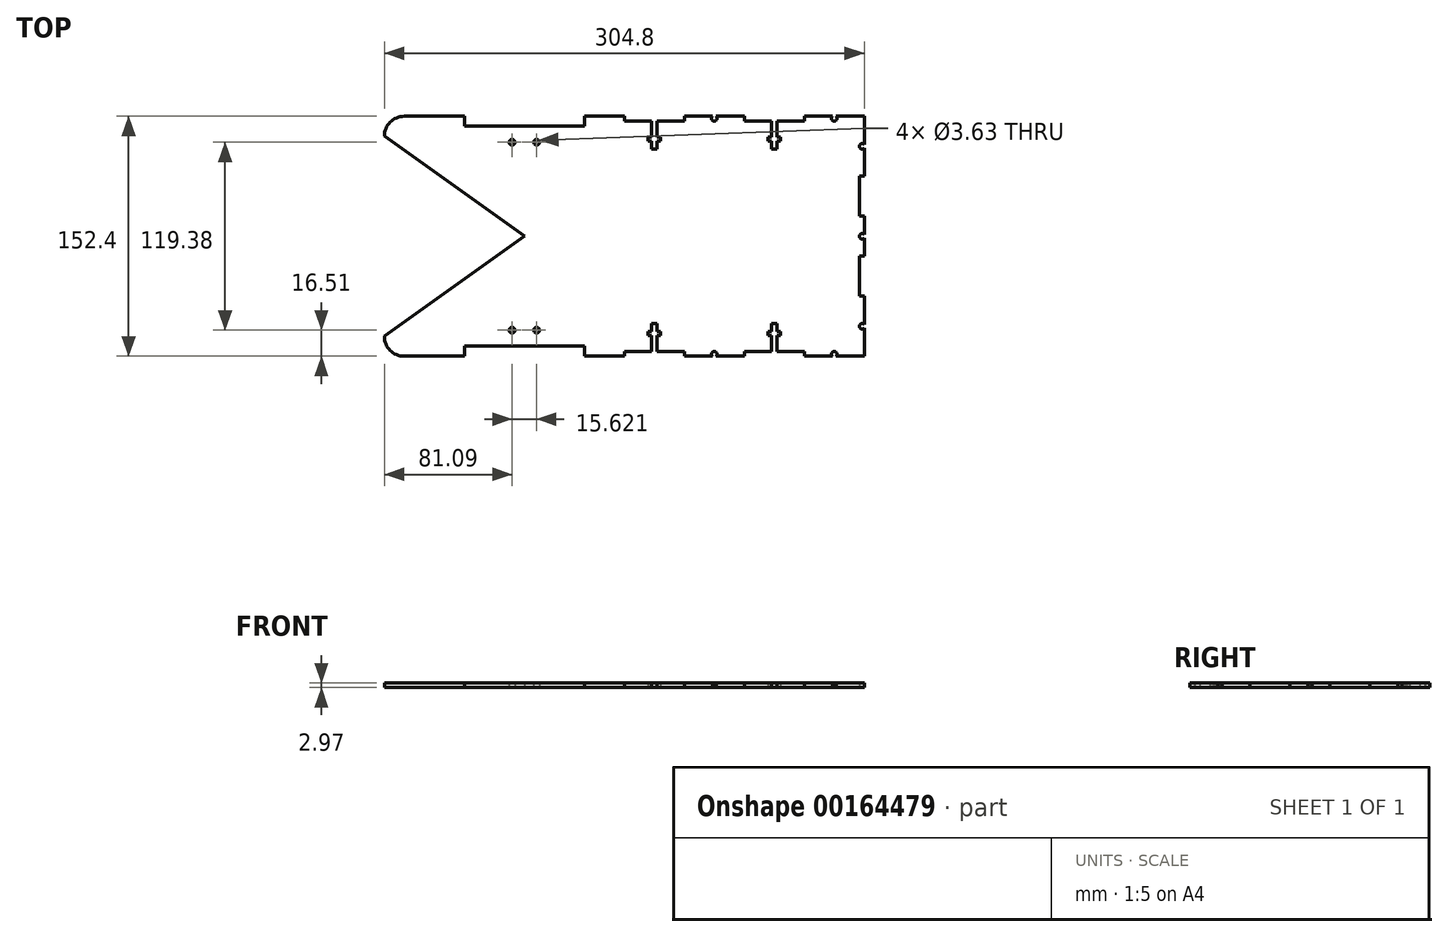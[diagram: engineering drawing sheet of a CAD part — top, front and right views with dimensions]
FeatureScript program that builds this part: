
annotation { "Feature Type Name" : "Feature", "Feature Type Description" : "" }
export const myFeature = defineFeature(function(context is Context, id is Id, definition is map)
    precondition{}
    {
        {
            var Q0;
            Q0=qCreatedBy(makeId("Top.planeOp"),FACE);
            var sketch = newSketch(context, id + "F0", { "sketchPlane" : qUnion([Q0])});
            skLineSegment(sketch, "E0.bottom", {"start": v(152.4, -76.2) * mm, "end": v(-139.7, -76.2) * mm});
            skLineSegment(sketch, "E0.top", {"start": v(152.4, 76.2) * mm, "end": v(-139.7, 76.2) * mm});
            skLineSegment(sketch, "E0.left", {"start": v(152.4, -76.2) * mm, "end": v(152.4, 76.2) * mm});
            skLineSegment(sketch, "E0.right", {"start": v(-152.4, -63.5) * mm, "end": v(-152.4, 63.5) * mm});
            skPoint(sketch, "E0.middle", {"position": v(0, 0) * mm});
            skLineSegment(sketch, "E1.bottom", {"start": v(-101.6, -76.2) * mm, "end": v(-25.4, -76.2) * mm});
            skLineSegment(sketch, "E1.top", {"start": v(-101.6, -69.85) * mm, "end": v(-25.4, -69.85) * mm});
            skLineSegment(sketch, "E1.left", {"start": v(-101.6, -76.2) * mm, "end": v(-101.6, -69.85) * mm});
            skLineSegment(sketch, "E1.right", {"start": v(-25.4, -76.2) * mm, "end": v(-25.4, -69.85) * mm});
            skLineSegment(sketch, "E2.bottom", {"start": v(0, -73.23) * mm, "end": v(17.28, -73.23) * mm});
            skLineSegment(sketch, "E2.top", {"start": v(0, -76.2) * mm, "end": v(38.1, -76.2) * mm});
            skLineSegment(sketch, "E2.left", {"start": v(0, -73.23) * mm, "end": v(0, -76.2) * mm});
            skLineSegment(sketch, "E2.right", {"start": v(38.1, -73.23) * mm, "end": v(38.1, -76.2) * mm});
            skLineSegment(sketch, "E3.bottom", {"start": v(17.28, -55.4) * mm, "end": v(20.82, -55.4) * mm});
            skLineSegment(sketch, "E3.top", {"start": v(17.28, -76.2) * mm, "end": v(20.82, -76.2) * mm});
            skLineSegment(sketch, "E3.left", {"start": v(17.28, -55.4) * mm, "end": v(17.28, -60.43) * mm});
            skLineSegment(sketch, "E3.right", {"start": v(20.82, -55.4) * mm, "end": v(20.82, -60.43) * mm});
            skPoint(sketch, "E4", {"position": v(19.05, -76.2) * mm});
            skLineSegment(sketch, "E5", {"start": v(19.05, -76.2) * mm, "end": v(19.05, -50.32) * mm, "construction": true});
            skLineSegment(sketch, "E6.bottom", {"start": v(22.94, -63.07) * mm, "end": v(20.82, -63.07) * mm});
            skLineSegment(sketch, "E6.top", {"start": v(22.94, -60.43) * mm, "end": v(20.82, -60.43) * mm});
            skLineSegment(sketch, "E6.left", {"start": v(22.94, -63.07) * mm, "end": v(22.94, -60.43) * mm});
            skLineSegment(sketch, "E6.right", {"start": v(15.16, -63.07) * mm, "end": v(15.16, -60.43) * mm});
            skPoint(sketch, "E6.middle", {"position": v(19.05, -61.75) * mm});
            skLineSegment(sketch, "E7.trimOffspring", {"start": v(20.82, -73.23) * mm, "end": v(38.1, -73.23) * mm});
            skLineSegment(sketch, "E8.trimOffspring", {"start": v(20.82, -63.07) * mm, "end": v(20.82, -73.23) * mm});
            skLineSegment(sketch, "E9.trimOffspring", {"start": v(17.28, -60.43) * mm, "end": v(15.16, -60.43) * mm});
            skLineSegment(sketch, "E10.trimOffspring", {"start": v(17.28, -63.07) * mm, "end": v(17.28, -73.23) * mm});
            skLineSegment(sketch, "E11.trimOffspring", {"start": v(17.28, -63.07) * mm, "end": v(15.16, -63.07) * mm});
            skArc(sketch, "E12", {"start": v(58.4, -76.2) * mm, "mid": v(57.15, -73.15) * mm, "end": v(55.9, -76.2) * mm});
            skLineSegment(sketch, "E13.1.0.0", {"start": v(93.48, -55.4) * mm, "end": v(93.48, -60.43) * mm});
            skPoint(sketch, "E13.1.0.1", {"position": v(95.25, -61.75) * mm});
            skLineSegment(sketch, "E13.1.0.2", {"start": v(97.02, -55.4) * mm, "end": v(97.02, -60.43) * mm});
            skArc(sketch, "E13.1.0.3", {"start": v(134.6, -76.2) * mm, "mid": v(133.35, -73.15) * mm, "end": v(132.1, -76.2) * mm});
            skLineSegment(sketch, "E13.1.0.4", {"start": v(93.48, -63.07) * mm, "end": v(93.48, -73.23) * mm});
            skLineSegment(sketch, "E13.1.0.5", {"start": v(97.02, -73.23) * mm, "end": v(114.3, -73.23) * mm});
            skLineSegment(sketch, "E13.1.0.6", {"start": v(76.2, -73.23) * mm, "end": v(93.48, -73.23) * mm});
            skLineSegment(sketch, "E13.1.0.7", {"start": v(76.2, -76.2) * mm, "end": v(114.3, -76.2) * mm});
            skLineSegment(sketch, "E13.1.0.8", {"start": v(97.02, -63.07) * mm, "end": v(97.02, -73.23) * mm});
            skLineSegment(sketch, "E13.1.0.9", {"start": v(95.25, -76.2) * mm, "end": v(95.25, -50.32) * mm, "construction": true});
            skPoint(sketch, "E13.1.0.10", {"position": v(95.25, -76.2) * mm});
            skLineSegment(sketch, "E13.1.0.11", {"start": v(93.48, -76.2) * mm, "end": v(97.02, -76.2) * mm});
            skLineSegment(sketch, "E13.1.0.12", {"start": v(99.14, -63.07) * mm, "end": v(97.02, -63.07) * mm});
            skLineSegment(sketch, "E13.1.0.13", {"start": v(99.14, -63.07) * mm, "end": v(99.14, -60.43) * mm});
            skLineSegment(sketch, "E13.1.0.14", {"start": v(91.36, -63.07) * mm, "end": v(91.36, -60.43) * mm});
            skLineSegment(sketch, "E13.1.0.15", {"start": v(93.48, -60.43) * mm, "end": v(91.36, -60.43) * mm});
            skLineSegment(sketch, "E13.1.0.16", {"start": v(99.14, -60.43) * mm, "end": v(97.02, -60.43) * mm});
            skLineSegment(sketch, "E13.1.0.17", {"start": v(76.2, -73.23) * mm, "end": v(76.2, -76.2) * mm});
            skLineSegment(sketch, "E13.1.0.18", {"start": v(114.3, -73.23) * mm, "end": v(114.3, -76.2) * mm});
            skLineSegment(sketch, "E13.1.0.19", {"start": v(93.48, -55.4) * mm, "end": v(97.02, -55.4) * mm});
            skLineSegment(sketch, "E13.1.0.20", {"start": v(93.48, -63.07) * mm, "end": v(91.36, -63.07) * mm});
            skLineSegment(sketch, "E13.direction1", {"start": v(0, -76.2) * mm, "end": v(76.2, -76.2) * mm, "construction": true});
            skLineSegment(sketch, "E14.MirrorCS", {"start": v(22.94, 63.07) * mm, "end": v(20.82, 63.07) * mm});
            skLineSegment(sketch, "E15.MirrorCS", {"start": v(22.94, 63.07) * mm, "end": v(22.94, 60.43) * mm});
            skLineSegment(sketch, "E16.MirrorCS", {"start": v(15.16, 63.07) * mm, "end": v(15.16, 60.43) * mm});
            skLineSegment(sketch, "E17.MirrorCS", {"start": v(17.28, 60.43) * mm, "end": v(15.16, 60.43) * mm});
            skLineSegment(sketch, "E18.MirrorCS", {"start": v(22.94, 60.43) * mm, "end": v(20.82, 60.43) * mm});
            skLineSegment(sketch, "E19.MirrorCS", {"start": v(99.14, 63.07) * mm, "end": v(99.14, 60.43) * mm});
            skLineSegment(sketch, "E20.MirrorCS", {"start": v(17.28, 63.07) * mm, "end": v(15.16, 63.07) * mm});
            skLineSegment(sketch, "E21.MirrorCS", {"start": v(99.14, 60.43) * mm, "end": v(97.02, 60.43) * mm});
            skLineSegment(sketch, "E22.MirrorCS", {"start": v(99.14, 63.07) * mm, "end": v(97.02, 63.07) * mm});
            skLineSegment(sketch, "E23.MirrorCS", {"start": v(93.48, 60.43) * mm, "end": v(91.36, 60.43) * mm});
            skLineSegment(sketch, "E24.MirrorCS", {"start": v(20.82, 55.4) * mm, "end": v(20.82, 60.43) * mm});
            skLineSegment(sketch, "E25.MirrorCS", {"start": v(76.2, 73.23) * mm, "end": v(76.2, 76.2) * mm});
            skLineSegment(sketch, "E26.MirrorCS", {"start": v(17.28, 55.4) * mm, "end": v(17.28, 60.43) * mm});
            skLineSegment(sketch, "E27.MirrorCS", {"start": v(0, 73.23) * mm, "end": v(0, 76.2) * mm});
            skLineSegment(sketch, "E28.MirrorCS", {"start": v(91.36, 63.07) * mm, "end": v(91.36, 60.43) * mm});
            skLineSegment(sketch, "E29.MirrorCS", {"start": v(93.48, 63.07) * mm, "end": v(91.36, 63.07) * mm});
            skLineSegment(sketch, "E30.MirrorCS", {"start": v(93.48, 55.4) * mm, "end": v(93.48, 60.43) * mm});
            skLineSegment(sketch, "E31.MirrorCS", {"start": v(97.02, 55.4) * mm, "end": v(97.02, 60.43) * mm});
            skLineSegment(sketch, "E32.MirrorCS", {"start": v(93.48, 55.4) * mm, "end": v(97.02, 55.4) * mm});
            skLineSegment(sketch, "E33.MirrorCS", {"start": v(-101.6, 76.2) * mm, "end": v(-101.6, 69.85) * mm});
            skLineSegment(sketch, "E34.MirrorCS", {"start": v(-25.4, 76.2) * mm, "end": v(-25.4, 69.85) * mm});
            skLineSegment(sketch, "E35.MirrorCS", {"start": v(38.1, 73.23) * mm, "end": v(38.1, 76.2) * mm});
            skLineSegment(sketch, "E36.MirrorCS", {"start": v(93.48, 76.2) * mm, "end": v(97.02, 76.2) * mm});
            skLineSegment(sketch, "E37.MirrorCS", {"start": v(114.3, 73.23) * mm, "end": v(114.3, 76.2) * mm});
            skLineSegment(sketch, "E38.MirrorCS", {"start": v(17.28, 55.4) * mm, "end": v(20.82, 55.4) * mm});
            skLineSegment(sketch, "E39.MirrorCS", {"start": v(17.28, 76.2) * mm, "end": v(20.82, 76.2) * mm});
            skLineSegment(sketch, "E40.MirrorCS", {"start": v(0, 76.2) * mm, "end": v(38.1, 76.2) * mm});
            skArc(sketch, "E41.MirrorCS", {"start": v(58.4, 76.2) * mm, "mid": v(57.15, 73.15) * mm, "end": v(55.9, 76.2) * mm});
            skArc(sketch, "E42.MirrorCS", {"start": v(134.6, 76.2) * mm, "mid": v(133.35, 73.15) * mm, "end": v(132.1, 76.2) * mm});
            skLineSegment(sketch, "E43.MirrorCS", {"start": v(97.02, 63.07) * mm, "end": v(97.02, 73.23) * mm});
            skLineSegment(sketch, "E44.MirrorCS", {"start": v(97.02, 73.23) * mm, "end": v(114.3, 73.23) * mm});
            skLineSegment(sketch, "E45.MirrorCS", {"start": v(20.82, 63.07) * mm, "end": v(20.82, 73.23) * mm});
            skPoint(sketch, "E46.MirrorP", {"position": v(95.25, 61.75) * mm});
            skPoint(sketch, "E47.MirrorP", {"position": v(19.05, 76.2) * mm});
            skLineSegment(sketch, "E48.MirrorCS", {"start": v(76.2, 76.2) * mm, "end": v(114.3, 76.2) * mm});
            skLineSegment(sketch, "E49.MirrorCS", {"start": v(93.48, 63.07) * mm, "end": v(93.48, 73.23) * mm});
            skLineSegment(sketch, "E50.MirrorCS", {"start": v(0, 76.2) * mm, "end": v(76.2, 76.2) * mm, "construction": true});
            skLineSegment(sketch, "E51.MirrorCS", {"start": v(20.82, 73.23) * mm, "end": v(38.1, 73.23) * mm});
            skLineSegment(sketch, "E52.MirrorCS", {"start": v(17.28, 63.07) * mm, "end": v(17.28, 73.23) * mm});
            skLineSegment(sketch, "E53.MirrorCS", {"start": v(76.2, 73.23) * mm, "end": v(93.48, 73.23) * mm});
            skPoint(sketch, "E54.MirrorP", {"position": v(95.25, 76.2) * mm});
            skLineSegment(sketch, "E55.MirrorCS", {"start": v(-101.6, 76.2) * mm, "end": v(-25.4, 76.2) * mm});
            skLineSegment(sketch, "E56.MirrorCS", {"start": v(-101.6, 69.85) * mm, "end": v(-25.4, 69.85) * mm});
            skLineSegment(sketch, "E57.MirrorCS", {"start": v(0, 73.23) * mm, "end": v(17.28, 73.23) * mm});
            skLineSegment(sketch, "E58.MirrorCS", {"start": v(19.05, 76.2) * mm, "end": v(19.05, 50.32) * mm, "construction": true});
            skPoint(sketch, "E59.MirrorP", {"position": v(19.05, 61.75) * mm});
            skLineSegment(sketch, "E60.MirrorCS", {"start": v(95.25, 76.2) * mm, "end": v(95.25, 50.32) * mm, "construction": true});
            skPoint(sketch, "E61.visualSharp", {"position": v(-152.4, 76.2) * mm});
            skArc(sketch, "E61.filletArc", {"start": v(-139.7, 76.2) * mm, "mid": v(-148.68, 72.48) * mm, "end": v(-152.4, 63.5) * mm});
            skPoint(sketch, "E62.visualSharp", {"position": v(-152.4, -76.2) * mm});
            skArc(sketch, "E62.filletArc", {"start": v(-152.4, -63.5) * mm, "mid": v(-148.68, -72.48) * mm, "end": v(-139.7, -76.2) * mm});
            skArc(sketch, "E63", {"start": v(152.4, -55.9) * mm, "mid": v(149.35, -57.15) * mm, "end": v(152.4, -58.4) * mm});
            skArc(sketch, "E64", {"start": v(152.4, 58.4) * mm, "mid": v(149.35, 57.15) * mm, "end": v(152.4, 55.9) * mm});
            skCircle(sketch, "E65", {"center": v(151.13, 0) * mm, "radius": 1.78 * mm});
            skLineSegment(sketch, "E66.bottom", {"start": v(149.43, -12.7) * mm, "end": v(152.4, -12.7) * mm});
            skLineSegment(sketch, "E66.top", {"start": v(149.43, -38.1) * mm, "end": v(152.4, -38.1) * mm});
            skLineSegment(sketch, "E66.left", {"start": v(149.43, -12.7) * mm, "end": v(149.43, -38.1) * mm});
            skLineSegment(sketch, "E66.right", {"start": v(152.4, -12.7) * mm, "end": v(152.4, -38.1) * mm});
            skLineSegment(sketch, "E67.bottom", {"start": v(149.43, 38.1) * mm, "end": v(152.4, 38.1) * mm});
            skLineSegment(sketch, "E67.top", {"start": v(149.43, 12.7) * mm, "end": v(152.4, 12.7) * mm});
            skLineSegment(sketch, "E67.left", {"start": v(149.43, 38.1) * mm, "end": v(149.43, 12.7) * mm});
            skLineSegment(sketch, "E67.right", {"start": v(152.4, 38.1) * mm, "end": v(152.4, 12.7) * mm});
            skPoint(sketch, "E68", {"position": v(-63.5, 0) * mm});
            skLineSegment(sketch, "E69", {"start": v(-152.4, 63.5) * mm, "end": v(-63.5, 0) * mm});
            skLineSegment(sketch, "E70", {"start": v(-152.4, -63.5) * mm, "end": v(-63.5, 0) * mm});
            skPoint(sketch, "E71", {"position": v(-63.5, -76.2) * mm});
            skLineSegment(sketch, "E72", {"start": v(-63.5, -76.2) * mm, "end": v(-63.5, -25.4) * mm, "construction": true});
            skCircle(sketch, "E73", {"center": v(-71.31, -59.7) * mm, "radius": 1.82 * mm});
            skLineSegment(sketch, "E74", {"start": v(-71.31, -59.7) * mm, "end": v(-55.69, -59.7) * mm, "construction": true});
            skCircle(sketch, "E75", {"center": v(-55.69, -59.7) * mm, "radius": 1.82 * mm});
            skPoint(sketch, "E76", {"position": v(-63.5, -59.7) * mm});
            skLineSegment(sketch, "E77.MirrorCS", {"start": v(-71.31, 59.7) * mm, "end": v(-55.69, 59.7) * mm, "construction": true});
            skCircle(sketch, "E78.MirrorC", {"center": v(-71.31, 59.7) * mm, "radius": 1.82 * mm});
            skPoint(sketch, "E79.MirrorP", {"position": v(-63.5, 59.7) * mm});
            skCircle(sketch, "E80.MirrorC", {"center": v(-55.69, 59.7) * mm, "radius": 1.82 * mm});
            skLineSegment(sketch, "E81.MirrorCS", {"start": v(-63.5, 76.2) * mm, "end": v(-63.5, 25.4) * mm, "construction": true});
            skSolve(sketch);
        }
        {
            var Q0;
            Q0=makeQuery(id+"F0.imprint","IMPRINT",FACE,{"disambiguationData":[TD([[makeQuery(id+"F0.imprint","IMPRINT",EDGE,{"derivedFrom":sQuery(id+"F0.wireOp",EDGE,"E1.top")}),1.0]])]});
            extrude(context, id + "F1", {"entities" : qUnion([Q0]), "depth" : 2.97 * mm});
        }
    });
